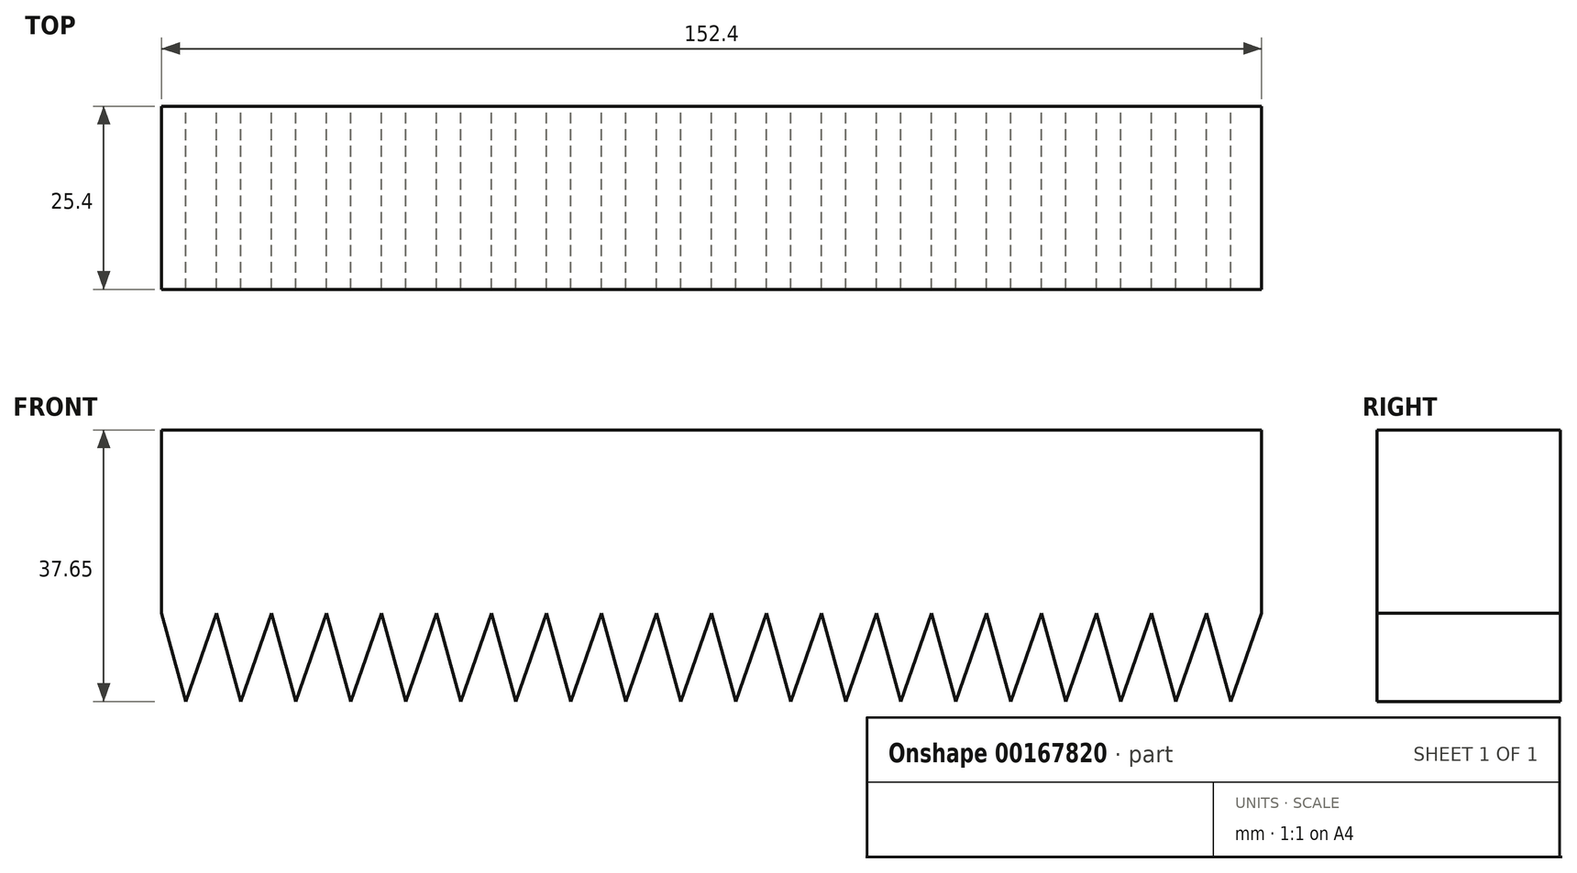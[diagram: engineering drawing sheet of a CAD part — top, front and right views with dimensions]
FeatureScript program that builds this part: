
annotation { "Feature Type Name" : "Feature", "Feature Type Description" : "" }
export const myFeature = defineFeature(function(context is Context, id is Id, definition is map)
    precondition{}
    {
        {
            var Q0;
            Q0=qCreatedBy(makeId("Front.planeOp"),FACE);
            var sketch = newSketch(context, id + "F0", { "sketchPlane" : qUnion([Q0])});
            skLineSegment(sketch, "E0.bottom", {"start": v(76.2, 10.18) * mm, "end": v(-76.2, 10.18) * mm});
            skLineSegment(sketch, "E0.top", {"start": v(76.2, -15.22) * mm, "end": v(-76.2, -15.22) * mm});
            skLineSegment(sketch, "E0.left", {"start": v(76.2, 10.18) * mm, "end": v(76.2, -15.22) * mm});
            skLineSegment(sketch, "E0.right", {"start": v(-76.2, 10.18) * mm, "end": v(-76.2, -15.22) * mm});
            skPoint(sketch, "E0.middle", {"position": v(0, -2.52) * mm});
            skLineSegment(sketch, "E1", {"start": v(-76.2, -15.22) * mm, "end": v(-72.87, -27.47) * mm});
            skLineSegment(sketch, "E2", {"start": v(-72.87, -27.47) * mm, "end": v(-68.58, -15.22) * mm});
            skLineSegment(sketch, "E3.1.0.0", {"start": v(-65.25, -27.47) * mm, "end": v(-60.96, -15.22) * mm});
            skLineSegment(sketch, "E3.1.0.1", {"start": v(-68.58, -15.22) * mm, "end": v(-65.25, -27.47) * mm});
            skLineSegment(sketch, "E3.2.0.0", {"start": v(-57.63, -27.47) * mm, "end": v(-53.34, -15.22) * mm});
            skLineSegment(sketch, "E3.2.0.1", {"start": v(-60.96, -15.22) * mm, "end": v(-57.63, -27.47) * mm});
            skLineSegment(sketch, "E3.3.0.0", {"start": v(-50.01, -27.47) * mm, "end": v(-45.72, -15.22) * mm});
            skLineSegment(sketch, "E3.3.0.1", {"start": v(-53.34, -15.22) * mm, "end": v(-50.01, -27.47) * mm});
            skLineSegment(sketch, "E3.4.0.0", {"start": v(-42.4, -27.47) * mm, "end": v(-38.1, -15.22) * mm});
            skLineSegment(sketch, "E3.4.0.1", {"start": v(-45.72, -15.22) * mm, "end": v(-42.4, -27.47) * mm});
            skLineSegment(sketch, "E3.5.0.0", {"start": v(-34.77, -27.47) * mm, "end": v(-30.48, -15.22) * mm});
            skLineSegment(sketch, "E3.5.0.1", {"start": v(-38.1, -15.22) * mm, "end": v(-34.77, -27.47) * mm});
            skLineSegment(sketch, "E3.6.0.0", {"start": v(-27.15, -27.47) * mm, "end": v(-22.86, -15.22) * mm});
            skLineSegment(sketch, "E3.6.0.1", {"start": v(-30.48, -15.22) * mm, "end": v(-27.15, -27.47) * mm});
            skLineSegment(sketch, "E3.7.0.0", {"start": v(-19.53, -27.47) * mm, "end": v(-15.24, -15.22) * mm});
            skLineSegment(sketch, "E3.7.0.1", {"start": v(-22.86, -15.22) * mm, "end": v(-19.53, -27.47) * mm});
            skLineSegment(sketch, "E3.8.0.0", {"start": v(-11.91, -27.47) * mm, "end": v(-7.62, -15.22) * mm});
            skLineSegment(sketch, "E3.8.0.1", {"start": v(-15.24, -15.22) * mm, "end": v(-11.91, -27.47) * mm});
            skLineSegment(sketch, "E3.9.0.0", {"start": v(-4.3, -27.47) * mm, "end": v(0, -15.22) * mm});
            skLineSegment(sketch, "E3.9.0.1", {"start": v(-7.62, -15.22) * mm, "end": v(-4.3, -27.47) * mm});
            skLineSegment(sketch, "E3.10.0.0", {"start": v(3.33, -27.47) * mm, "end": v(7.62, -15.22) * mm});
            skLineSegment(sketch, "E3.10.0.1", {"start": v(0, -15.22) * mm, "end": v(3.33, -27.47) * mm});
            skLineSegment(sketch, "E3.11.0.0", {"start": v(10.95, -27.47) * mm, "end": v(15.24, -15.22) * mm});
            skLineSegment(sketch, "E3.11.0.1", {"start": v(7.62, -15.22) * mm, "end": v(10.95, -27.47) * mm});
            skLineSegment(sketch, "E3.12.0.0", {"start": v(18.57, -27.47) * mm, "end": v(22.86, -15.22) * mm});
            skLineSegment(sketch, "E3.12.0.1", {"start": v(15.24, -15.22) * mm, "end": v(18.57, -27.47) * mm});
            skLineSegment(sketch, "E3.13.0.0", {"start": v(26.19, -27.47) * mm, "end": v(30.48, -15.22) * mm});
            skLineSegment(sketch, "E3.13.0.1", {"start": v(22.86, -15.22) * mm, "end": v(26.19, -27.47) * mm});
            skLineSegment(sketch, "E3.14.0.0", {"start": v(33.8, -27.47) * mm, "end": v(38.1, -15.22) * mm});
            skLineSegment(sketch, "E3.14.0.1", {"start": v(30.48, -15.22) * mm, "end": v(33.8, -27.47) * mm});
            skLineSegment(sketch, "E3.15.0.0", {"start": v(41.43, -27.47) * mm, "end": v(45.72, -15.22) * mm});
            skLineSegment(sketch, "E3.15.0.1", {"start": v(38.1, -15.22) * mm, "end": v(41.43, -27.47) * mm});
            skLineSegment(sketch, "E3.16.0.0", {"start": v(49.05, -27.47) * mm, "end": v(53.34, -15.22) * mm});
            skLineSegment(sketch, "E3.16.0.1", {"start": v(45.72, -15.22) * mm, "end": v(49.05, -27.47) * mm});
            skLineSegment(sketch, "E3.17.0.0", {"start": v(56.67, -27.47) * mm, "end": v(60.96, -15.22) * mm});
            skLineSegment(sketch, "E3.17.0.1", {"start": v(53.34, -15.22) * mm, "end": v(56.67, -27.47) * mm});
            skLineSegment(sketch, "E3.18.0.0", {"start": v(64.29, -27.47) * mm, "end": v(68.58, -15.22) * mm});
            skLineSegment(sketch, "E3.18.0.1", {"start": v(60.96, -15.22) * mm, "end": v(64.29, -27.47) * mm});
            skLineSegment(sketch, "E3.19.0.0", {"start": v(71.9, -27.47) * mm, "end": v(76.2, -15.22) * mm});
            skLineSegment(sketch, "E3.19.0.1", {"start": v(68.58, -15.22) * mm, "end": v(71.9, -27.47) * mm});
            skLineSegment(sketch, "E3.direction1", {"start": v(-72.87, -27.47) * mm, "end": v(-65.25, -27.47) * mm, "construction": true});
            skSolve(sketch);
        }
        {
            var Q0;
            {var subQ0=sQuery(id+"F0.wireOp",EDGE,"E3.19.0.0");Q0=makeQuery(id+"F0.imprint","IMPRINT",FACE,{"disambiguationData":[TD([[makeQuery(id+"F0.imprint","IMPRINT",EDGE,{"derivedFrom":subQ0}),1.0]])]});}
            var Q1;
            {var subQ2=sQuery(id+"F0.wireOp",EDGE,"E3.18.0.0");Q1=makeQuery(id+"F0.imprint","IMPRINT",FACE,{"disambiguationData":[TD([[makeQuery(id+"F0.imprint","IMPRINT",EDGE,{"derivedFrom":subQ2}),1.0]])]});}
            var Q2;
            {var subQ2=sQuery(id+"F0.wireOp",EDGE,"E3.17.0.0");Q2=makeQuery(id+"F0.imprint","IMPRINT",FACE,{"disambiguationData":[TD([[makeQuery(id+"F0.imprint","IMPRINT",EDGE,{"derivedFrom":subQ2}),1.0]])]});}
            var Q3;
            {var subQ2=sQuery(id+"F0.wireOp",EDGE,"E3.16.0.0");Q3=makeQuery(id+"F0.imprint","IMPRINT",FACE,{"disambiguationData":[TD([[makeQuery(id+"F0.imprint","IMPRINT",EDGE,{"derivedFrom":subQ2}),1.0]])]});}
            var Q4;
            {var subQ2=sQuery(id+"F0.wireOp",EDGE,"E3.15.0.0");Q4=makeQuery(id+"F0.imprint","IMPRINT",FACE,{"disambiguationData":[TD([[makeQuery(id+"F0.imprint","IMPRINT",EDGE,{"derivedFrom":subQ2}),1.0]])]});}
            var Q5;
            {var subQ2=sQuery(id+"F0.wireOp",EDGE,"E3.14.0.0");Q5=makeQuery(id+"F0.imprint","IMPRINT",FACE,{"disambiguationData":[TD([[makeQuery(id+"F0.imprint","IMPRINT",EDGE,{"derivedFrom":subQ2}),1.0]])]});}
            var Q6;
            {var subQ2=sQuery(id+"F0.wireOp",EDGE,"E3.13.0.0");Q6=makeQuery(id+"F0.imprint","IMPRINT",FACE,{"disambiguationData":[TD([[makeQuery(id+"F0.imprint","IMPRINT",EDGE,{"derivedFrom":subQ2}),1.0]])]});}
            var Q7;
            {var subQ2=sQuery(id+"F0.wireOp",EDGE,"E3.12.0.0");Q7=makeQuery(id+"F0.imprint","IMPRINT",FACE,{"disambiguationData":[TD([[makeQuery(id+"F0.imprint","IMPRINT",EDGE,{"derivedFrom":subQ2}),1.0]])]});}
            var Q8;
            {var subQ2=sQuery(id+"F0.wireOp",EDGE,"E3.11.0.0");Q8=makeQuery(id+"F0.imprint","IMPRINT",FACE,{"disambiguationData":[TD([[makeQuery(id+"F0.imprint","IMPRINT",EDGE,{"derivedFrom":subQ2}),1.0]])]});}
            var Q9;
            {var subQ2=sQuery(id+"F0.wireOp",EDGE,"E3.10.0.0");Q9=makeQuery(id+"F0.imprint","IMPRINT",FACE,{"disambiguationData":[TD([[makeQuery(id+"F0.imprint","IMPRINT",EDGE,{"derivedFrom":subQ2}),1.0]])]});}
            var Q10;
            {var subQ2=sQuery(id+"F0.wireOp",EDGE,"E3.9.0.0");Q10=makeQuery(id+"F0.imprint","IMPRINT",FACE,{"disambiguationData":[TD([[makeQuery(id+"F0.imprint","IMPRINT",EDGE,{"derivedFrom":subQ2}),1.0]])]});}
            var Q11;
            {var subQ2=sQuery(id+"F0.wireOp",EDGE,"E3.8.0.0");Q11=makeQuery(id+"F0.imprint","IMPRINT",FACE,{"disambiguationData":[TD([[makeQuery(id+"F0.imprint","IMPRINT",EDGE,{"derivedFrom":subQ2}),1.0]])]});}
            var Q12;
            {var subQ2=sQuery(id+"F0.wireOp",EDGE,"E3.7.0.0");Q12=makeQuery(id+"F0.imprint","IMPRINT",FACE,{"disambiguationData":[TD([[makeQuery(id+"F0.imprint","IMPRINT",EDGE,{"derivedFrom":subQ2}),1.0]])]});}
            var Q13;
            {var subQ2=sQuery(id+"F0.wireOp",EDGE,"E3.6.0.0");Q13=makeQuery(id+"F0.imprint","IMPRINT",FACE,{"disambiguationData":[TD([[makeQuery(id+"F0.imprint","IMPRINT",EDGE,{"derivedFrom":subQ2}),1.0]])]});}
            var Q14;
            {var subQ2=sQuery(id+"F0.wireOp",EDGE,"E3.5.0.0");Q14=makeQuery(id+"F0.imprint","IMPRINT",FACE,{"disambiguationData":[TD([[makeQuery(id+"F0.imprint","IMPRINT",EDGE,{"derivedFrom":subQ2}),1.0]])]});}
            var Q15;
            {var subQ2=sQuery(id+"F0.wireOp",EDGE,"E3.4.0.0");Q15=makeQuery(id+"F0.imprint","IMPRINT",FACE,{"disambiguationData":[TD([[makeQuery(id+"F0.imprint","IMPRINT",EDGE,{"derivedFrom":subQ2}),1.0]])]});}
            var Q16;
            {var subQ2=sQuery(id+"F0.wireOp",EDGE,"E3.3.0.0");Q16=makeQuery(id+"F0.imprint","IMPRINT",FACE,{"disambiguationData":[TD([[makeQuery(id+"F0.imprint","IMPRINT",EDGE,{"derivedFrom":subQ2}),1.0]])]});}
            var Q17;
            {var subQ2=sQuery(id+"F0.wireOp",EDGE,"E3.2.0.0");Q17=makeQuery(id+"F0.imprint","IMPRINT",FACE,{"disambiguationData":[TD([[makeQuery(id+"F0.imprint","IMPRINT",EDGE,{"derivedFrom":subQ2}),1.0]])]});}
            var Q18;
            {var subQ2=sQuery(id+"F0.wireOp",EDGE,"E3.1.0.0");Q18=makeQuery(id+"F0.imprint","IMPRINT",FACE,{"disambiguationData":[TD([[makeQuery(id+"F0.imprint","IMPRINT",EDGE,{"derivedFrom":subQ2}),1.0]])]});}
            var Q19;
            {var subQ0=sQuery(id+"F0.wireOp",EDGE,"E1");Q19=makeQuery(id+"F0.imprint","IMPRINT",FACE,{"disambiguationData":[TD([[makeQuery(id+"F0.imprint","IMPRINT",EDGE,{"derivedFrom":subQ0}),1.0]])]});}
            var Q20;
            Q20=makeQuery(id+"F0.imprint","IMPRINT",FACE,{"disambiguationData":[TD([[makeQuery(id+"F0.imprint","IMPRINT",EDGE,{"derivedFrom":sQuery(id+"F0.wireOp",EDGE,"E0.bottom")}),1.0]])]});
            extrude(context, id + "F1", {"entities" : qUnion([Q0, Q1, Q2, Q3, Q4, Q5, Q6, Q7, Q8, Q9, Q10, Q11, Q12, Q13, Q14, Q15, Q16, Q17, Q18, Q19, Q20]), "endBound" : BoundingType.SYMMETRIC, "depth" : 25.4 * mm});
        }
    });
